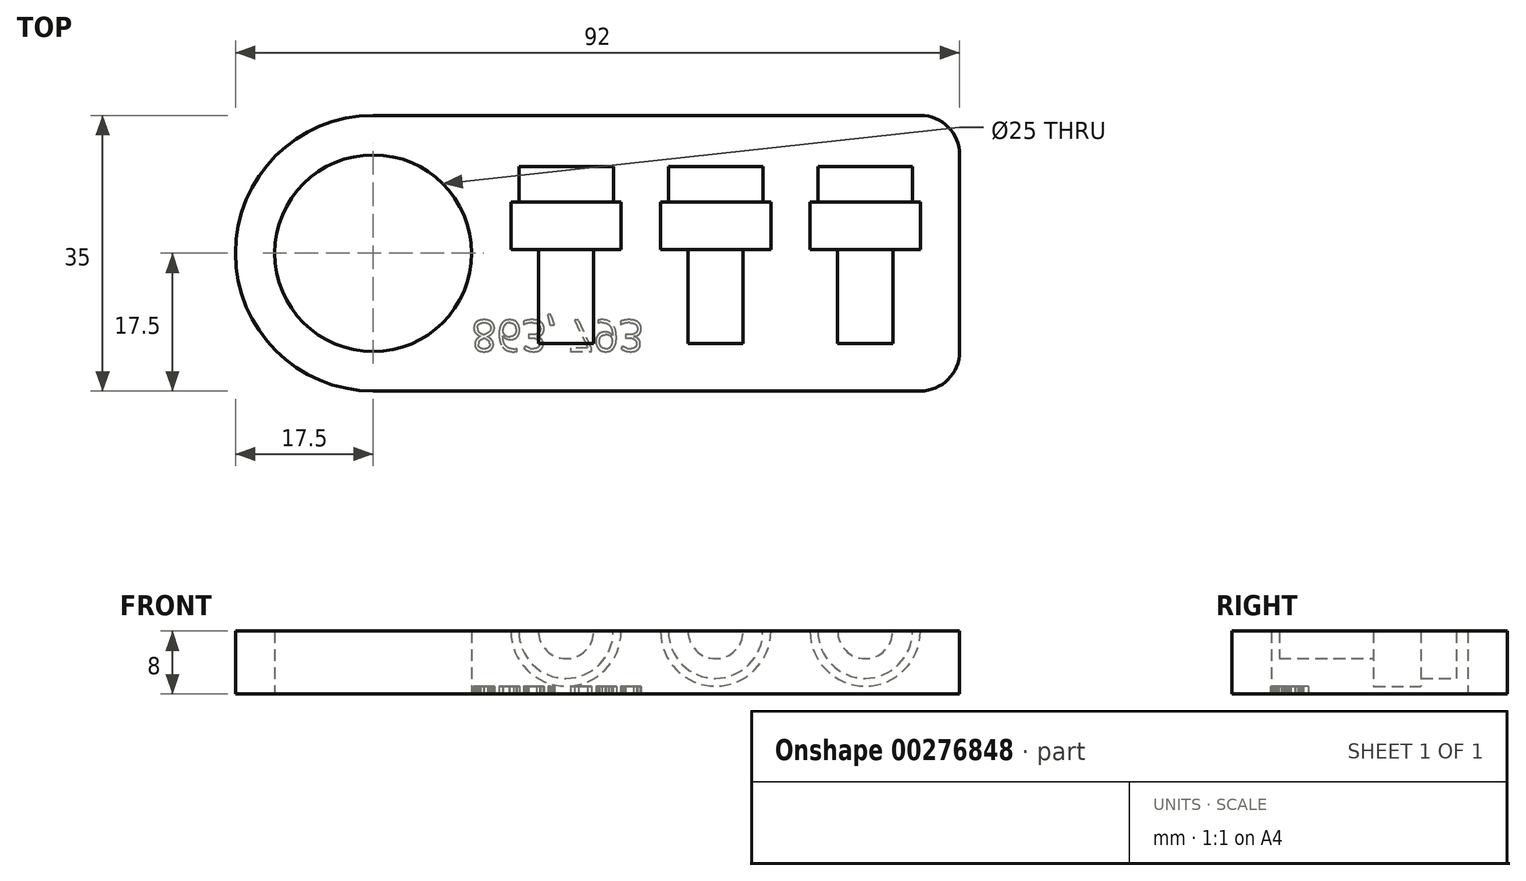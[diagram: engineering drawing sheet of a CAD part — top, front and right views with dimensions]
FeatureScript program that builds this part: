
annotation { "Feature Type Name" : "Feature", "Feature Type Description" : "" }
export const myFeature = defineFeature(function(context is Context, id is Id, definition is map)
    precondition{}
    {
        {
            var Q0;
            Q0=qCreatedBy(makeId("Top.planeOp"),FACE);
            var sketch = newSketch(context, id + "F0", { "sketchPlane" : qUnion([Q0])});
            skLineSegment(sketch, "E0.bottom", {"start": v(17.5, 0) * mm, "end": v(87, 0) * mm});
            skLineSegment(sketch, "E0.top", {"start": v(17.5, 35) * mm, "end": v(87, 35) * mm});
            skLineSegment(sketch, "E0.left", {"start": v(0, 17.5) * mm, "end": v(0, 17.5) * mm});
            skLineSegment(sketch, "E0.right", {"start": v(92, 5) * mm, "end": v(92, 30) * mm});
            skLineSegment(sketch, "E1.bottom", {"start": v(0, 0) * mm, "end": v(17.5, 0) * mm, "construction": true});
            skLineSegment(sketch, "E1.top", {"start": v(0, 17.5) * mm, "end": v(17.5, 17.5) * mm, "construction": true});
            skLineSegment(sketch, "E1.left", {"start": v(0, 0) * mm, "end": v(0, 17.5) * mm, "construction": true});
            skLineSegment(sketch, "E1.right", {"start": v(17.5, 0) * mm, "end": v(17.5, 17.5) * mm, "construction": true});
            skCircle(sketch, "E2", {"center": v(17.5, 17.5) * mm, "radius": 12.5 * mm});
            skPoint(sketch, "E3.visualSharp", {"position": v(0, 0) * mm});
            skArc(sketch, "E3.filletArc", {"start": v(0, 17.5) * mm, "mid": v(5.13, 5.13) * mm, "end": v(17.5, 0) * mm});
            skPoint(sketch, "E4.visualSharp", {"position": v(0, 35) * mm});
            skArc(sketch, "E4.filletArc", {"start": v(17.5, 35) * mm, "mid": v(5.13, 29.87) * mm, "end": v(0, 17.5) * mm});
            skPoint(sketch, "E5.visualSharp", {"position": v(92, 35) * mm});
            skArc(sketch, "E5.filletArc", {"start": v(92, 30) * mm, "mid": v(90.54, 33.54) * mm, "end": v(87, 35) * mm});
            skPoint(sketch, "E6.visualSharp", {"position": v(92, 0) * mm});
            skArc(sketch, "E6.filletArc", {"start": v(87, 0) * mm, "mid": v(90.54, 1.46) * mm, "end": v(92, 5) * mm});
            skSolve(sketch);
        }
        {
            var Q0;
            Q0=makeQuery(id+"F0.imprint","IMPRINT",FACE,{"disambiguationData":[TD([[makeQuery(id+"F0.imprint","IMPRINT",EDGE,{"derivedFrom":sQuery(id+"F0.wireOp",EDGE,"E0.bottom")}),1.0]])]});
            extrude(context, id + "F1", {"entities" : qUnion([Q0]), "depth" : 8 * mm});
        }
        {
            var Q0;
            Q0=makeQuery(id+"F1.opExtrude","CAP_FACE",FACE,{"disambiguationData":[OSD([sQuery(id+"F0.wireOp",EDGE,"E0.bottom"),sQuery(id+"F0.wireOp",EDGE,"E0.top"),sQuery(id+"F0.wireOp",EDGE,"E0.right"),sQuery(id+"F0.wireOp",EDGE,"E2"),sQuery(id+"F0.wireOp",EDGE,"E3.filletArc"),sQuery(id+"F0.wireOp",EDGE,"E4.filletArc"),sQuery(id+"F0.wireOp",EDGE,"E5.filletArc"),sQuery(id+"F0.wireOp",EDGE,"E6.filletArc")])],"isStart":false});
            var sketch = newSketch(context, id + "F2", { "sketchPlane" : qUnion([Q0])});
            skLineSegment(sketch, "E7.bottom", {"start": v(0, 0) * mm, "end": v(42, 0) * mm, "construction": true});
            skLineSegment(sketch, "E7.top", {"start": v(0, 6) * mm, "end": v(42, 6) * mm, "construction": true});
            skLineSegment(sketch, "E7.left", {"start": v(0, 0) * mm, "end": v(0, 6) * mm, "construction": true});
            skLineSegment(sketch, "E7.right", {"start": v(42, 0) * mm, "end": v(42, 6) * mm, "construction": true});
            skLineSegment(sketch, "E8", {"start": v(42, 6) * mm, "end": v(61, 6) * mm, "construction": true});
            skLineSegment(sketch, "E9", {"start": v(61, 6) * mm, "end": v(80, 6) * mm, "construction": true});
            skLineSegment(sketch, "E10.bottom", {"start": v(42, 6) * mm, "end": v(45.5, 6) * mm});
            skLineSegment(sketch, "E10.left", {"start": v(42, 6) * mm, "end": v(42, 18) * mm});
            skLineSegment(sketch, "E10.right", {"start": v(45.5, 6) * mm, "end": v(45.5, 18) * mm});
            skLineSegment(sketch, "E11.bottom", {"start": v(61, 6) * mm, "end": v(64.5, 6) * mm});
            skLineSegment(sketch, "E11.left", {"start": v(61, 6) * mm, "end": v(61, 18) * mm});
            skLineSegment(sketch, "E11.right", {"start": v(64.5, 6) * mm, "end": v(64.5, 18) * mm});
            skLineSegment(sketch, "E12.bottom", {"start": v(80, 6) * mm, "end": v(83.5, 6) * mm});
            skLineSegment(sketch, "E12.left", {"start": v(80, 6) * mm, "end": v(80, 18) * mm});
            skLineSegment(sketch, "E12.right", {"start": v(83.5, 6) * mm, "end": v(83.5, 18) * mm});
            skLineSegment(sketch, "E13.bottom", {"start": v(45.5, 18) * mm, "end": v(49, 18) * mm});
            skLineSegment(sketch, "E13.top", {"start": v(48, 24) * mm, "end": v(49, 24) * mm});
            skLineSegment(sketch, "E13.left", {"start": v(42, 18) * mm, "end": v(42, 24) * mm});
            skLineSegment(sketch, "E13.right", {"start": v(49, 18) * mm, "end": v(49, 24) * mm});
            skLineSegment(sketch, "E14.bottom", {"start": v(64.5, 18) * mm, "end": v(68, 18) * mm});
            skLineSegment(sketch, "E14.top", {"start": v(67, 24) * mm, "end": v(68, 24) * mm});
            skLineSegment(sketch, "E14.left", {"start": v(61, 18) * mm, "end": v(61, 24) * mm});
            skLineSegment(sketch, "E14.right", {"start": v(68, 18) * mm, "end": v(68, 24) * mm});
            skLineSegment(sketch, "E15.bottom", {"start": v(83.5, 18) * mm, "end": v(87, 18) * mm});
            skLineSegment(sketch, "E15.top", {"start": v(86, 24) * mm, "end": v(87, 24) * mm});
            skLineSegment(sketch, "E15.left", {"start": v(80, 18) * mm, "end": v(80, 24) * mm});
            skLineSegment(sketch, "E15.right", {"start": v(87, 18) * mm, "end": v(87, 24) * mm});
            skLineSegment(sketch, "E16.top", {"start": v(42, 28.5) * mm, "end": v(48, 28.5) * mm});
            skLineSegment(sketch, "E16.left", {"start": v(42, 24) * mm, "end": v(42, 28.5) * mm});
            skLineSegment(sketch, "E16.right", {"start": v(48, 24) * mm, "end": v(48, 28.5) * mm});
            skLineSegment(sketch, "E17.top", {"start": v(61, 28.5) * mm, "end": v(67, 28.5) * mm});
            skLineSegment(sketch, "E17.left", {"start": v(61, 24) * mm, "end": v(61, 28.5) * mm});
            skLineSegment(sketch, "E17.right", {"start": v(67, 24) * mm, "end": v(67, 28.5) * mm});
            skLineSegment(sketch, "E18.top", {"start": v(80, 28.5) * mm, "end": v(86, 28.5) * mm});
            skLineSegment(sketch, "E18.left", {"start": v(80, 24) * mm, "end": v(80, 28.5) * mm});
            skLineSegment(sketch, "E18.right", {"start": v(86, 24) * mm, "end": v(86, 28.5) * mm});
            skSolve(sketch);
        }
        {
            var Q0;
            Q0=makeQuery(id+"F2.imprint","IMPRINT",FACE,{"disambiguationData":[TD([[makeQuery(id+"F2.imprint","IMPRINT",EDGE,{"derivedFrom":sQuery(id+"F2.wireOp",EDGE,"E10.bottom")}),1.0]])]});
            var Q1;
            Q1=sQuery(id+"F2.wireOp",EDGE,"E10.left");
            revolve(context, id + "F3", {"operationType" : NewBodyOperationType.REMOVE, "entities" : qUnion([Q0]), "axis" : qUnion([Q1]), "revolveType" : RevolveType.FULL, "oppositeDirection" : true});
        }
        {
            var Q0;
            Q0=makeQuery(id+"F2.imprint","IMPRINT",FACE,{"disambiguationData":[TD([[makeQuery(id+"F2.imprint","IMPRINT",EDGE,{"derivedFrom":sQuery(id+"F2.wireOp",EDGE,"E11.bottom")}),1.0]])]});
            var Q1;
            Q1=sQuery(id+"F2.wireOp",EDGE,"E11.left");
            revolve(context, id + "F4", {"operationType" : NewBodyOperationType.REMOVE, "entities" : qUnion([Q0]), "axis" : qUnion([Q1]), "revolveType" : RevolveType.FULL, "oppositeDirection" : true});
        }
        {
            var Q0;
            Q0=makeQuery(id+"F2.imprint","IMPRINT",FACE,{"disambiguationData":[TD([[makeQuery(id+"F2.imprint","IMPRINT",EDGE,{"derivedFrom":sQuery(id+"F2.wireOp",EDGE,"E12.bottom")}),1.0]])]});
            var Q1;
            Q1=sQuery(id+"F2.wireOp",EDGE,"E12.left");
            revolve(context, id + "F5", {"operationType" : NewBodyOperationType.REMOVE, "entities" : qUnion([Q0]), "axis" : qUnion([Q1]), "revolveType" : RevolveType.FULL, "oppositeDirection" : true});
        }
        {
            var Q0;
            Q0=makeQuery(id+"F1.opExtrude","CAP_FACE",FACE,{"disambiguationData":[OSD([sQuery(id+"F0.wireOp",EDGE,"E0.bottom"),sQuery(id+"F0.wireOp",EDGE,"E0.top"),sQuery(id+"F0.wireOp",EDGE,"E0.right"),sQuery(id+"F0.wireOp",EDGE,"E2"),sQuery(id+"F0.wireOp",EDGE,"E3.filletArc"),sQuery(id+"F0.wireOp",EDGE,"E4.filletArc"),sQuery(id+"F0.wireOp",EDGE,"E5.filletArc"),sQuery(id+"F0.wireOp",EDGE,"E6.filletArc")])],"isStart":true});
            var sketch = newSketch(context, id + "F6", { "sketchPlane" : qUnion([Q0])});
            skLineSegment(sketch, "E19.bottom", {"start": v(0, 0) * mm, "end": v(30, 0) * mm, "construction": true});
            skLineSegment(sketch, "E19.top", {"start": v(0, -5) * mm, "end": v(30, -5) * mm, "construction": true});
            skLineSegment(sketch, "E19.left", {"start": v(0, 0) * mm, "end": v(0, -5) * mm, "construction": true});
            skLineSegment(sketch, "E19.right", {"start": v(30, 0) * mm, "end": v(30, -5) * mm, "construction": true});
            skText(sketch, "E20", { "text": "863, 793", "fontName": "OpenSans-Regular.ttf"});
            const initialGuessF6  = {"E20": [0.03, -0.009, 1, 0, 0.004]};
            skSetInitialGuess(sketch, initialGuessF6);
            skSolve(sketch);
        }
        {
            var Q0;
            Q0 = qSketchRegion(id + "F6", true);
            extrude(context, id + "F7", {"entities" : qUnion([Q0]), "operationType" : NewBodyOperationType.REMOVE, "oppositeDirection" : true, "depth" : 1 * mm});
        }
    });
